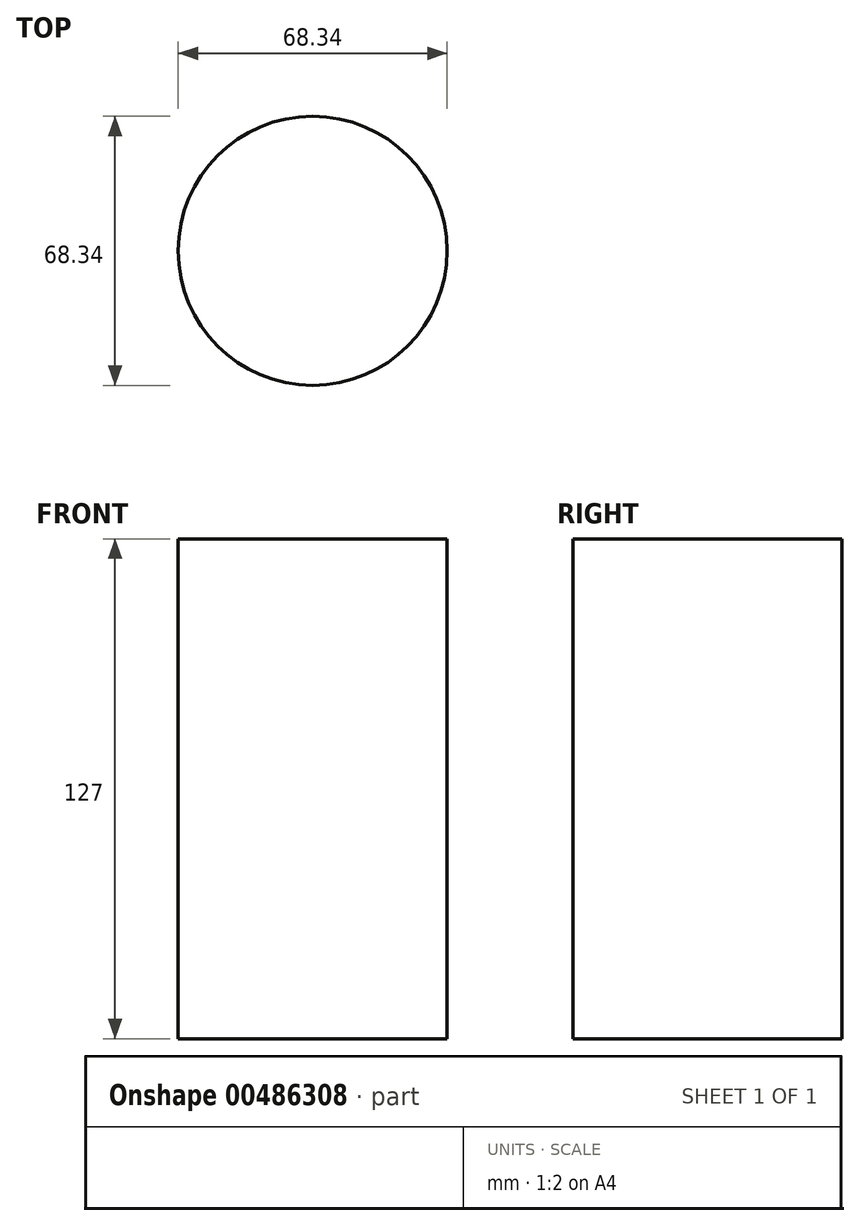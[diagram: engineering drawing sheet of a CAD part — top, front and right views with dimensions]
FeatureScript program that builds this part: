
annotation { "Feature Type Name" : "Feature", "Feature Type Description" : "" }
export const myFeature = defineFeature(function(context is Context, id is Id, definition is map)
    precondition{}
    {
        {
            var Q0;
            Q0=qCreatedBy(makeId("Top.planeOp"),FACE);
            var sketch = newSketch(context, id + "F0", { "sketchPlane" : qUnion([Q0])});
            skCircle(sketch, "E0", {"center": v(0, 0) * mm, "radius": 34.17 * mm});
            skSolve(sketch);
        }
        {
            var Q0;
            Q0=makeQuery(id+"F0.imprint","IMPRINT",FACE,{"disambiguationData":[TD([[makeQuery(id+"F0.imprint","IMPRINT",EDGE,{"derivedFrom":sQuery(id+"F0.wireOp",EDGE,"E0")}),1.0]])]});
            var Q1;
            Q1=sQuery(id+"F0.wireOp",EDGE,"E0");
            extrude(context, id + "F1", {"entities" : qUnion([Q0]), "surfaceEntities" : qUnion([Q1]), "depth" : 127 * mm});
        }
    });
